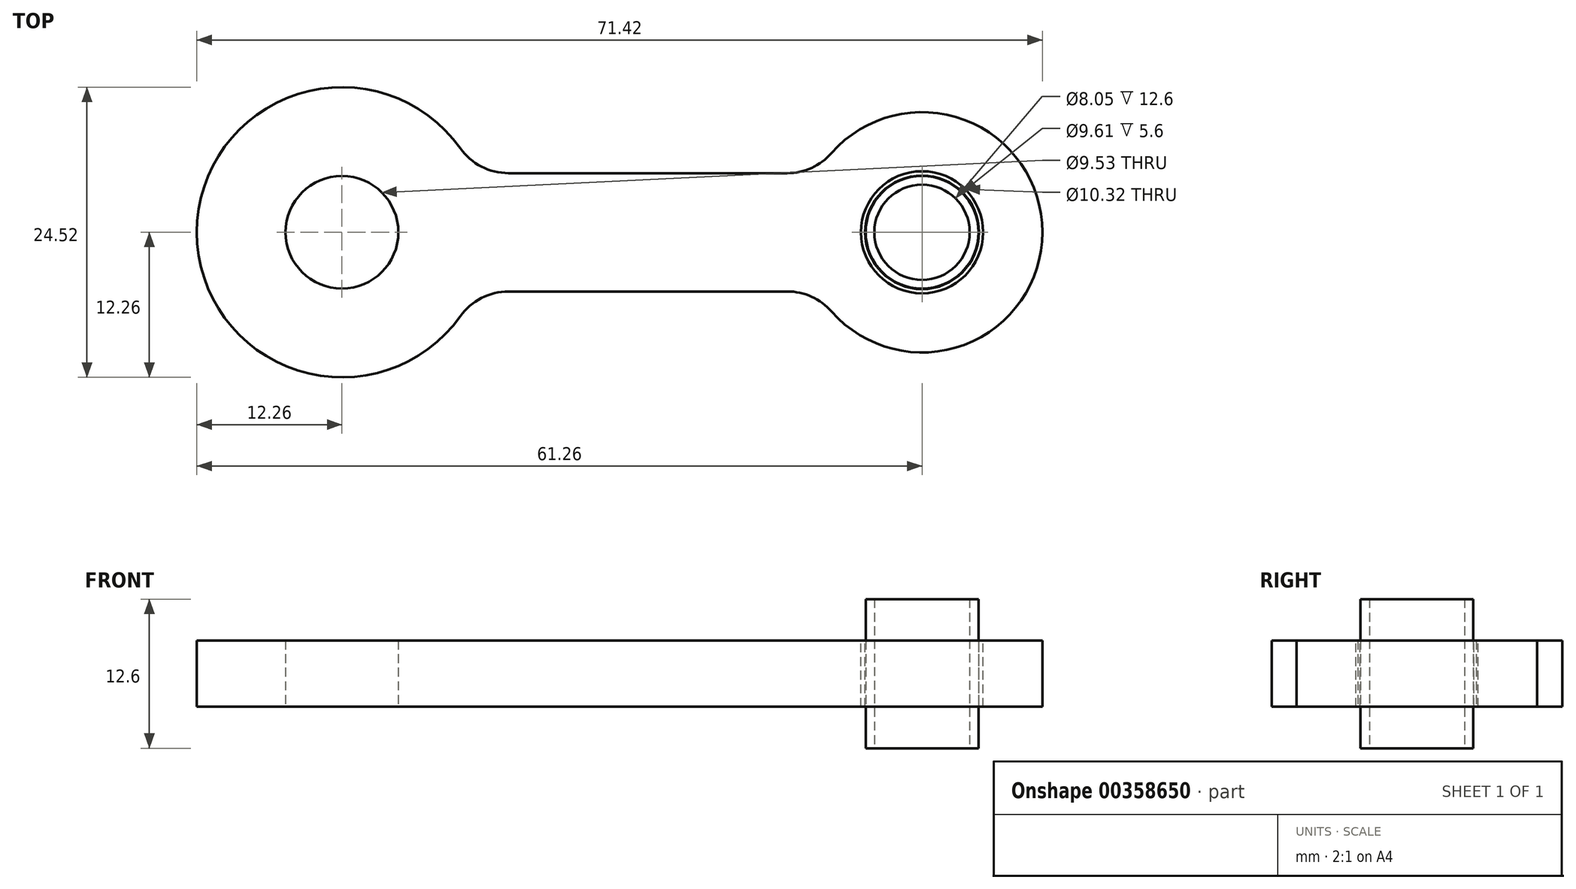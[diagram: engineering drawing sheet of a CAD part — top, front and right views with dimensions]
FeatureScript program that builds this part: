
annotation { "Feature Type Name" : "Feature", "Feature Type Description" : "" }
export const myFeature = defineFeature(function(context is Context, id is Id, definition is map)
    precondition{}
    {
        {
            var Q0;
            Q0=qCreatedBy(makeId("Top.planeOp"),FACE);
            var sketch = newSketch(context, id + "F0", { "sketchPlane" : qUnion([Q0])});
            skCircle(sketch, "E0", {"center": v(0, 0) * mm, "radius": 4.76 * mm});
            skArc(sketch, "E1", {"start": v(10, 7.1) * mm, "mid": v(-12.26, 0) * mm, "end": v(10, -7.1) * mm});
            skCircle(sketch, "E2", {"center": v(49, 0) * mm, "radius": 5.16 * mm});
            skLineSegment(sketch, "E3", {"start": v(0, 0) * mm, "end": v(49, 0) * mm, "construction": true});
            skLineSegment(sketch, "E4", {"start": v(14.07, -5) * mm, "end": v(37.6, -5) * mm});
            skArc(sketch, "E5", {"start": v(14.07, -5) * mm, "mid": v(11.78, -5.56) * mm, "end": v(10, -7.1) * mm});
            skLineSegment(sketch, "E6.trimOffspring", {"start": v(14.07, 5) * mm, "end": v(37.6, 5) * mm});
            skArc(sketch, "E7", {"start": v(10, 7.1) * mm, "mid": v(11.78, 5.56) * mm, "end": v(14.07, 5) * mm});
            skArc(sketch, "E8", {"start": v(41.36, -6.7) * mm, "mid": v(59.16, 0) * mm, "end": v(41.36, 6.7) * mm});
            skArc(sketch, "E9", {"start": v(37.6, 5) * mm, "mid": v(39.67, 5.45) * mm, "end": v(41.36, 6.7) * mm});
            skArc(sketch, "E10", {"start": v(41.36, -6.7) * mm, "mid": v(39.67, -5.45) * mm, "end": v(37.6, -5) * mm});
            skSolve(sketch);
        }
        {
            var Q0;
            Q0=makeQuery(id+"F0.imprint","IMPRINT",FACE,{"disambiguationData":[TD([[makeQuery(id+"F0.imprint","IMPRINT",EDGE,{"derivedFrom":sQuery(id+"F0.wireOp",EDGE,"E0")}),-1.0]])]});
            extrude(context, id + "F1", {"entities" : qUnion([Q0]), "depth" : 5.6 * mm, "offsetDistance" : 25 * mm});
        }
        {
            var Q0;
            Q0=makeQuery(id+"F1.opExtrude","CAP_FACE",FACE,{"disambiguationData":[OSD([sQuery(id+"F0.wireOp",EDGE,"E0"),sQuery(id+"F0.wireOp",EDGE,"E1"),sQuery(id+"F0.wireOp",EDGE,"E2"),sQuery(id+"F0.wireOp",EDGE,"E4"),sQuery(id+"F0.wireOp",EDGE,"E5"),sQuery(id+"F0.wireOp",EDGE,"E6.trimOffspring"),sQuery(id+"F0.wireOp",EDGE,"E7"),sQuery(id+"F0.wireOp",EDGE,"E8"),sQuery(id+"F0.wireOp",EDGE,"E9"),sQuery(id+"F0.wireOp",EDGE,"E10")])],"isStart":false});
            var sketch = newSketch(context, id + "F2", { "sketchPlane" : qUnion([Q0])});
            skCircle(sketch, "E11", {"center": v(49, 0) * mm, "radius": 5.16 * mm});
            skCircle(sketch, "E12", {"center": v(49, 0) * mm, "radius": 4.8 * mm});
            skSolve(sketch);
        }
        {
            var Q0;
            Q0 = qSketchRegion(id + "F2", true);
            extrude(context, id + "F3", {"entities" : qUnion([Q0]), "depth" : 0 * mm, "offsetDistance" : 25 * mm, "hasSecondDirection" : true, "secondDirectionOppositeDirection" : true, "secondDirectionDepth" : 5.6 * mm});
        }
        {
            var Q0;
            Q0=makeQuery(id+"F1.opExtrude","CAP_FACE",FACE,{"disambiguationData":[OSD([sQuery(id+"F0.wireOp",EDGE,"E0"),sQuery(id+"F0.wireOp",EDGE,"E1"),sQuery(id+"F0.wireOp",EDGE,"E2"),sQuery(id+"F0.wireOp",EDGE,"E4"),sQuery(id+"F0.wireOp",EDGE,"E5"),sQuery(id+"F0.wireOp",EDGE,"E6.trimOffspring"),sQuery(id+"F0.wireOp",EDGE,"E7"),sQuery(id+"F0.wireOp",EDGE,"E8"),sQuery(id+"F0.wireOp",EDGE,"E9"),sQuery(id+"F0.wireOp",EDGE,"E10")])],"isStart":false});
            var sketch = newSketch(context, id + "F4", { "sketchPlane" : qUnion([Q0])});
            skCircle(sketch, "E13", {"center": v(49, 0) * mm, "radius": 4.76 * mm});
            skCircle(sketch, "E14", {"center": v(49, 0) * mm, "radius": 4.03 * mm});
            skSolve(sketch);
        }
        {
            var Q0;
            Q0 = qSketchRegion(id + "F4", true);
            extrude(context, id + "F5", {"entities" : qUnion([Q0]), "depth" : 3.5 * mm, "offsetDistance" : 25 * mm, "hasSecondDirection" : true, "secondDirectionOppositeDirection" : true, "secondDirectionDepth" : (5.6 + 3.5) * mm});
        }
    });
